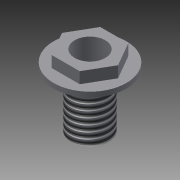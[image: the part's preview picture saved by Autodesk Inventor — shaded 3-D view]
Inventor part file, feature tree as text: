
AUTODESK INVENTOR PART (.ipt)
format: ipt  version: 2013 (Build 170138000, 138)  size: 104,960 bytes
history: native  units: mm
features: extrude x3, sketch x3, thread x1
ambient origin geometry x8: Origin, YZ Plane, XZ Plane, XY Plane, X Axis, Y Axis, Z Axis, Center Point
bodies: Solid1 (feature_tree)
feature tree (7):
  extrude  "Extrusion1"  Depth=6.25mm
  extrude  "Extrusion2"  Depth=9.9mm
  extrude  "Extrusion3"  Depth=14.8mm
  thread  "Thread1"  [1 undecoded]
  sketch  "Sketch1"  dims[d0=7.7mm d2=6.25mm]
  sketch  "Sketch2"  dims[d3=14.45mm d4=0.0mm d5=9.9mm]
  sketch  "Sketch3"  dims[d6=2.3mm d7=0.0mm d8=14.8mm d10=1.0mm d11=0.0mm d12=10.0mm d13=0.0mm]
note: 1 required parameter value undecoded (feature->parameter linkage not recoverable at this tier; creation-order binding heuristic only, values carry confidence <= 0.55)
